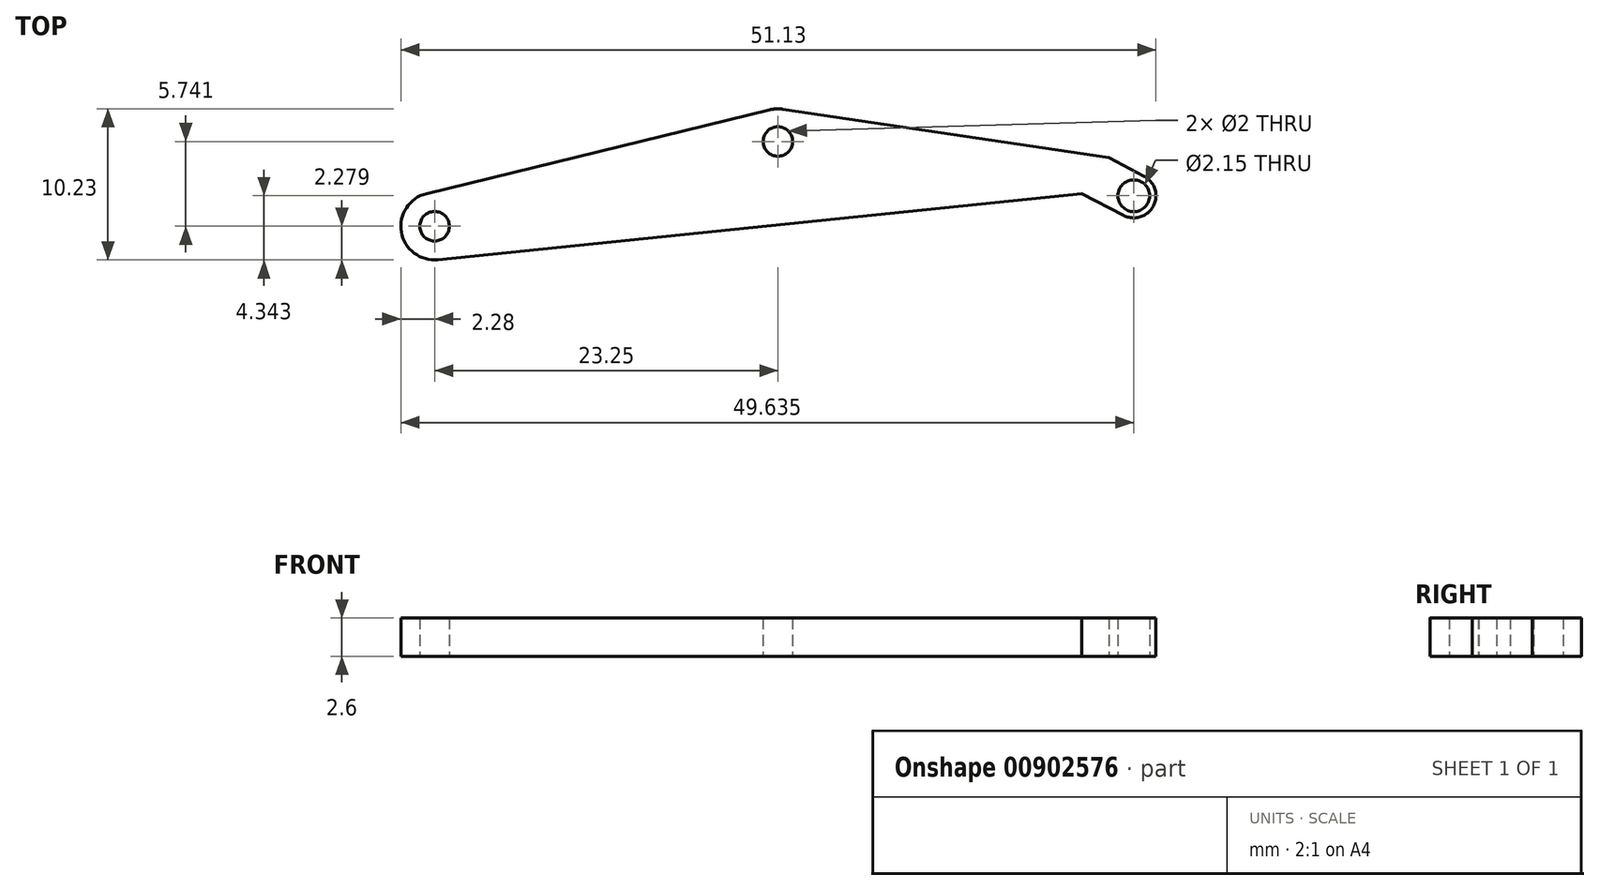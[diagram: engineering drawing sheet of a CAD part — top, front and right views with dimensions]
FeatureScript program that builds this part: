
annotation { "Feature Type Name" : "Feature", "Feature Type Description" : "" }
export const myFeature = defineFeature(function(context is Context, id is Id, definition is map)
    precondition{}
    {
        {
            var Q0;
            Q0=qCreatedBy(makeId("Top.planeOp"),FACE);
            var sketch = newSketch(context, id + "F0", { "sketchPlane" : qUnion([Q0])});
            skCircle(sketch, "E0", {"center": v(-1.2, 3.05) * mm, "radius": 2.21 * mm});
            skCircle(sketch, "E1", {"center": v(-24.45, -2.7) * mm, "radius": 2.28 * mm});
            skCircle(sketch, "E2", {"center": v(22.9, -0.63) * mm, "radius": 1.5 * mm});
            skLineSegment(sketch, "E3", {"start": v(-25, -0.48) * mm, "end": v(-1.72, 5.2) * mm});
            skLineSegment(sketch, "E4", {"start": v(21.22, 1.95) * mm, "end": v(23.6, 0.7) * mm});
            skLineSegment(sketch, "E5", {"start": v(-24.22, -4.96) * mm, "end": v(19.37, -0.47) * mm});
            skLineSegment(sketch, "E6", {"start": v(19.37, -0.47) * mm, "end": v(22.2, -1.96) * mm});
            skLineSegment(sketch, "E7", {"start": v(21.22, 1.95) * mm, "end": v(-0.87, 5.24) * mm});
            skCircle(sketch, "E8", {"center": v(-24.45, -2.7) * mm, "radius": 1 * mm});
            skCircle(sketch, "E9", {"center": v(-1.2, 3.05) * mm, "radius": 1 * mm});
            skCircle(sketch, "E10", {"center": v(22.9, -0.63) * mm, "radius": 1.07 * mm});
            skSolve(sketch);
        }
        {
            var Q0;
            Q0 = qSketchRegion(id + "F0", true);
            extrude(context, id + "F1", {"entities" : qUnion([Q0]), "depth" : 1.3 * mm, "offsetDistance" : 25 * mm});
        }
        {
            var Q0;
            Q0=makeQuery(id+"F1.opExtrude","SWEPT_BODY",BODY,{"disambiguationData":[OSD([sQuery(id+"F0.wireOp",EDGE,"E0"),sQuery(id+"F0.wireOp",EDGE,"E1"),sQuery(id+"F0.wireOp",EDGE,"E2"),sQuery(id+"F0.wireOp",EDGE,"E3"),sQuery(id+"F0.wireOp",EDGE,"E4"),sQuery(id+"F0.wireOp",EDGE,"E5"),sQuery(id+"F0.wireOp",EDGE,"E6"),sQuery(id+"F0.wireOp",EDGE,"E7"),sQuery(id+"F0.wireOp",EDGE,"E8"),sQuery(id+"F0.wireOp",EDGE,"E9")])]});
            var Q1;
            Q1=qCreatedBy(makeId("Top.planeOp"),FACE);
            mirror(context, id + "F2", {"operationType" : NewBodyOperationType.ADD, "entities" : qUnion([Q0]), "mirrorPlane" : qUnion([Q1])});
        }
    });
